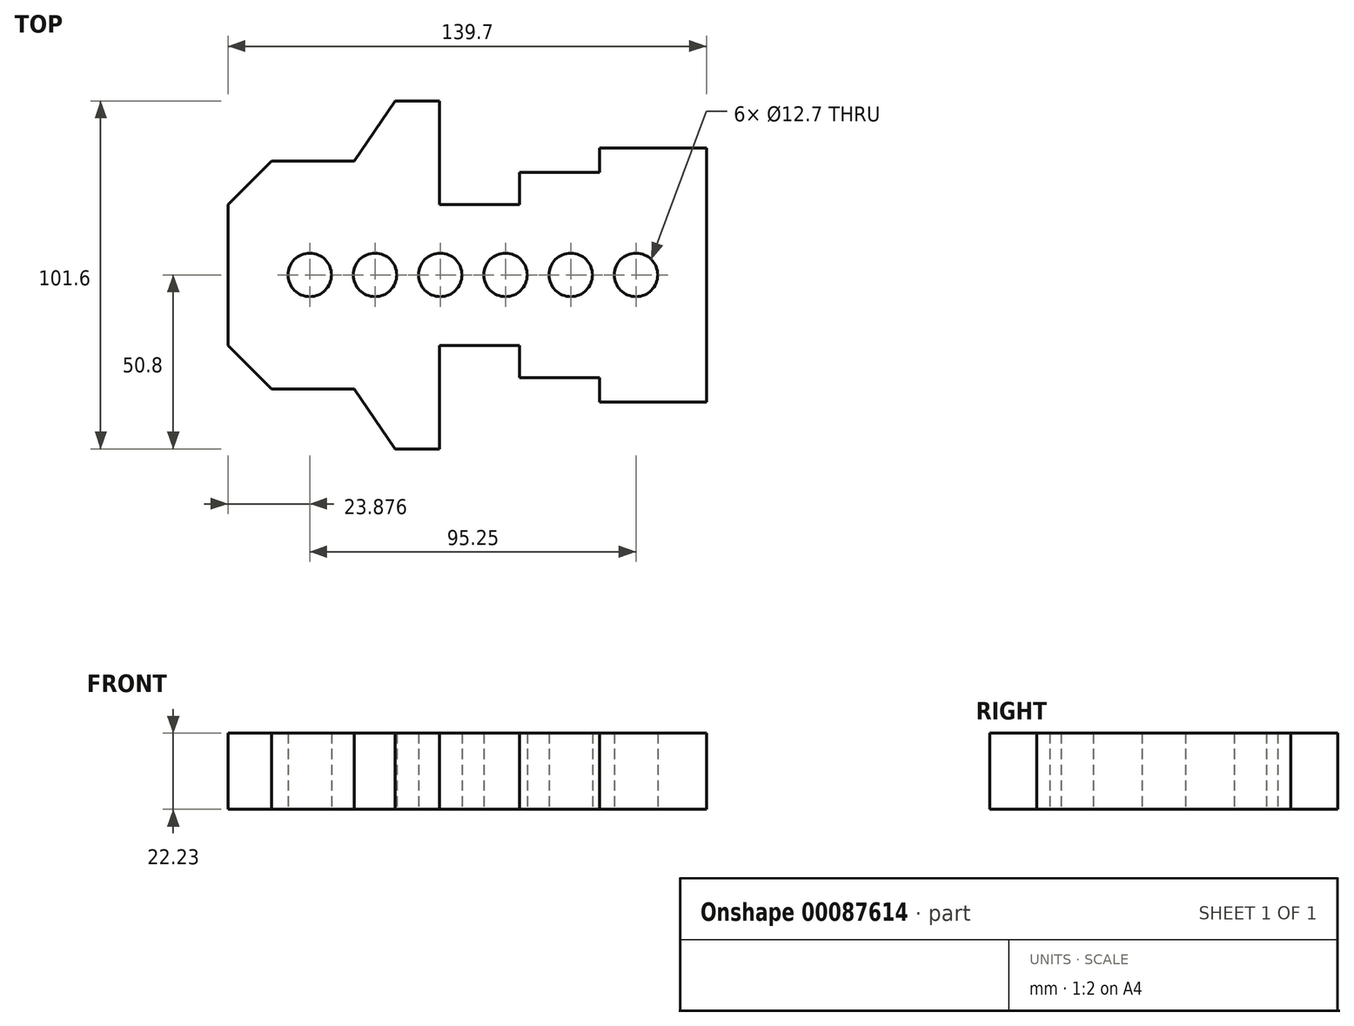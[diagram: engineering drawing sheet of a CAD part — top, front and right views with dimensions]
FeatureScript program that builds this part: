
annotation { "Feature Type Name" : "Feature", "Feature Type Description" : "" }
export const myFeature = defineFeature(function(context is Context, id is Id, definition is map)
    precondition{}
    {
        {
            var Q0;
            Q0=qCreatedBy(makeId("Top.planeOp"),FACE);
            var sketch = newSketch(context, id + "F0", { "sketchPlane" : qUnion([Q0])});
            skLineSegment(sketch, "E0", {"start": v(0, 0) * mm, "end": v(0, -20.57) * mm});
            skLineSegment(sketch, "E1", {"start": v(0, -20.57) * mm, "end": v(12.7, -33.27) * mm});
            skLineSegment(sketch, "E2", {"start": v(12.7, -33.27) * mm, "end": v(36.83, -33.27) * mm});
            skLineSegment(sketch, "E3", {"start": v(36.83, -33.27) * mm, "end": v(48.77, -50.8) * mm});
            skLineSegment(sketch, "E4", {"start": v(48.77, -50.8) * mm, "end": v(61.72, -50.8) * mm});
            skLineSegment(sketch, "E5", {"start": v(61.72, -50.8) * mm, "end": v(61.72, -20.57) * mm});
            skLineSegment(sketch, "E6", {"start": v(61.72, -20.57) * mm, "end": v(85.1, -20.57) * mm});
            skLineSegment(sketch, "E7", {"start": v(85.1, -20.57) * mm, "end": v(85.1, -29.97) * mm});
            skLineSegment(sketch, "E8", {"start": v(85.1, -29.97) * mm, "end": v(108.46, -29.97) * mm});
            skLineSegment(sketch, "E9", {"start": v(108.46, -29.97) * mm, "end": v(108.46, -37.08) * mm});
            skLineSegment(sketch, "E10", {"start": v(108.46, -37.08) * mm, "end": v(139.7, -37.08) * mm});
            skLineSegment(sketch, "E11", {"start": v(139.7, -37.08) * mm, "end": v(139.7, 0) * mm});
            skLineSegment(sketch, "E12", {"start": v(139.7, 0) * mm, "end": v(0, 0) * mm});
            skSolve(sketch);
        }
        {
            var Q0;
            Q0 = qSketchRegion(id + "F0", true);
            extrude(context, id + "F1", {"entities" : qUnion([Q0]), "depth" : 22.22 * mm});
        }
        {
            var Q0;
            Q0=makeQuery(id+"F1.opExtrude","SWEPT_BODY",BODY,{"disambiguationData":[OSD([sQuery(id+"F0.wireOp",EDGE,"E0"),sQuery(id+"F0.wireOp",EDGE,"E1"),sQuery(id+"F0.wireOp",EDGE,"E2"),sQuery(id+"F0.wireOp",EDGE,"E3"),sQuery(id+"F0.wireOp",EDGE,"E4"),sQuery(id+"F0.wireOp",EDGE,"E5"),sQuery(id+"F0.wireOp",EDGE,"E6"),sQuery(id+"F0.wireOp",EDGE,"E7"),sQuery(id+"F0.wireOp",EDGE,"E8"),sQuery(id+"F0.wireOp",EDGE,"E9"),sQuery(id+"F0.wireOp",EDGE,"E10"),sQuery(id+"F0.wireOp",EDGE,"E11"),sQuery(id+"F0.wireOp",EDGE,"E12")])]});
            var Q1;
            Q1=makeQuery(id+"F1.opExtrude","SWEPT_FACE",FACE,{"disambiguationData":[OSD([sQuery(id+"F0.wireOp",EDGE,"E12")])]});
            mirror(context, id + "F2", {"operationType" : NewBodyOperationType.ADD, "entities" : qUnion([Q0]), "mirrorPlane" : qUnion([Q1])});
        }
        {
            var Q0;
            Q0=qCreatedBy(makeId("Top.planeOp"),FACE);
            var sketch = newSketch(context, id + "F3", { "sketchPlane" : qUnion([Q0])});
            skCircle(sketch, "E13", {"center": v(23.88, 0) * mm, "radius": 6.35 * mm});
            skCircle(sketch, "E14.1.0.0", {"center": v(42.93, 0) * mm, "radius": 6.35 * mm});
            skCircle(sketch, "E14.2.0.0", {"center": v(61.98, 0) * mm, "radius": 6.35 * mm});
            skLineSegment(sketch, "E14.direction1", {"start": v(23.88, 0) * mm, "end": v(42.93, 0) * mm, "construction": true});
            skCircle(sketch, "E15.0.3.0", {"center": v(81.03, 0) * mm, "radius": 6.35 * mm});
            skCircle(sketch, "E15.0.4.0", {"center": v(100.08, 0) * mm, "radius": 6.35 * mm});
            skCircle(sketch, "E15.0.5.0", {"center": v(119.13, 0) * mm, "radius": 6.35 * mm});
            skSolve(sketch);
        }
        {
            var Q0;
            Q0 = qSketchRegion(id + "F3", true);
            extrude(context, id + "F4", {"entities" : qUnion([Q0]), "operationType" : NewBodyOperationType.REMOVE, "endBound" : BoundingType.THROUGH_ALL, "depth" : 25.4 * mm});
        }
    });
